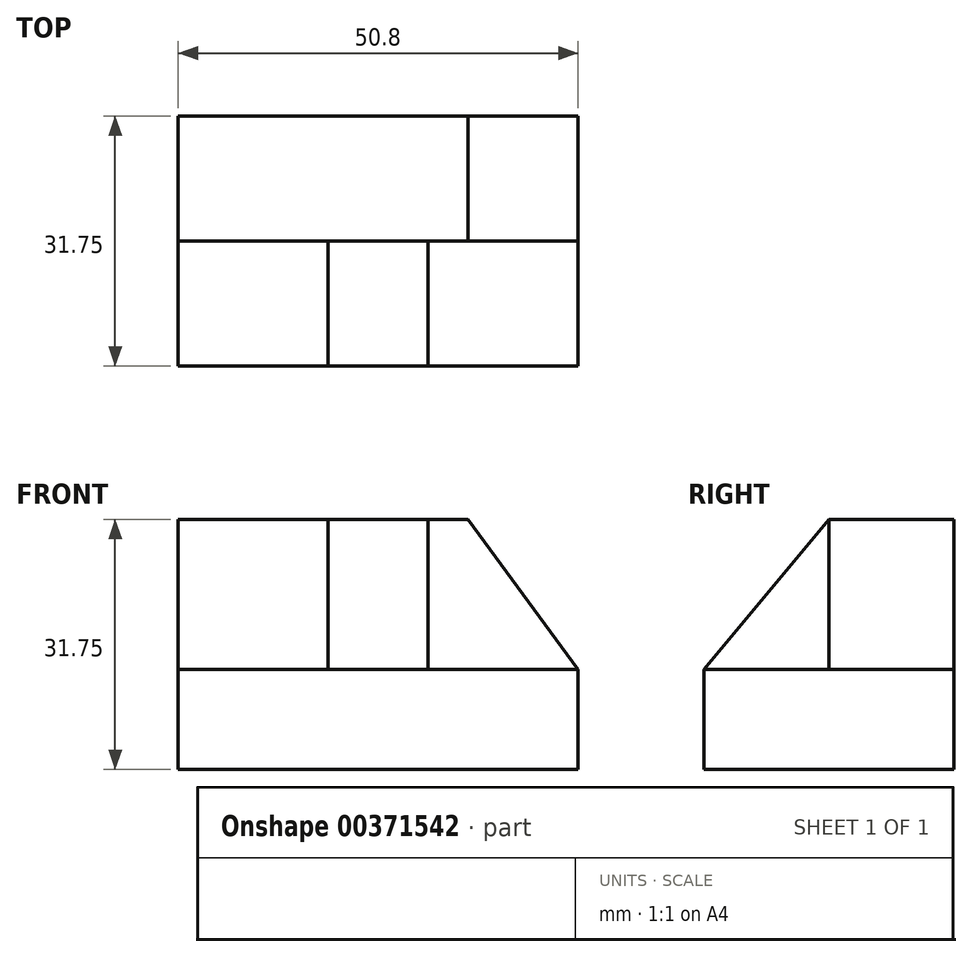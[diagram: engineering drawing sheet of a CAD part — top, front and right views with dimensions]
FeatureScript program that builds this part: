
annotation { "Feature Type Name" : "Feature", "Feature Type Description" : "" }
export const myFeature = defineFeature(function(context is Context, id is Id, definition is map)
    precondition{}
    {
        {
            var Q0;
            Q0=qCreatedBy(makeId("Front.planeOp"),FACE);
            var sketch = newSketch(context, id + "F0", { "sketchPlane" : qUnion([Q0])});
            skLineSegment(sketch, "E0", {"start": v(0, 0) * mm, "end": v(50.8, 0) * mm});
            skLineSegment(sketch, "E1", {"start": v(50.8, 0) * mm, "end": v(50.8, 31.75) * mm});
            skLineSegment(sketch, "E2", {"start": v(50.8, 31.75) * mm, "end": v(0, 31.75) * mm});
            skLineSegment(sketch, "E3", {"start": v(0, 31.75) * mm, "end": v(0, 0) * mm});
            skSolve(sketch);
        }
        {
            var Q0;
            Q0 = qSketchRegion(id + "F0", true);
            extrude(context, id + "F1", {"entities" : qUnion([Q0]), "depth" : 31.75 * mm});
        }
        {
            var Q0;
            Q0=makeQuery(id+"F1.opExtrude","SWEPT_FACE",FACE,{"disambiguationData":[OSD([sQuery(id+"F0.wireOp",EDGE,"E1")])]});
            var sketch = newSketch(context, id + "F2", { "sketchPlane" : qUnion([Q0])});
            skLineSegment(sketch, "E4", {"start": v(-15.88, 31.75) * mm, "end": v(-15.88, 12.7) * mm});
            skLineSegment(sketch, "E5", {"start": v(-15.88, 12.7) * mm, "end": v(-31.75, 12.7) * mm});
            skLineSegment(sketch, "E6", {"start": v(-31.75, 12.7) * mm, "end": v(-31.75, 31.75) * mm});
            skLineSegment(sketch, "E7", {"start": v(-31.75, 31.75) * mm, "end": v(-15.88, 31.75) * mm});
            skSolve(sketch);
        }
        {
            var Q0;
            Q0=makeQuery(id+"F1.opExtrude","SWEPT_FACE",FACE,{"disambiguationData":[OSD([sQuery(id+"F0.wireOp",EDGE,"E3")])]});
            var sketch = newSketch(context, id + "F3", { "sketchPlane" : qUnion([Q0])});
            skLineSegment(sketch, "E8", {"start": v(15.88, 31.75) * mm, "end": v(15.88, 12.7) * mm});
            skLineSegment(sketch, "E9", {"start": v(15.88, 12.7) * mm, "end": v(31.75, 12.7) * mm});
            skLineSegment(sketch, "E10", {"start": v(31.75, 12.7) * mm, "end": v(31.75, 31.75) * mm});
            skLineSegment(sketch, "E11", {"start": v(31.75, 31.75) * mm, "end": v(15.88, 31.75) * mm});
            skSolve(sketch);
        }
        {
            var Q0;
            Q0 = qSketchRegion(id + "F3", true);
            extrude(context, id + "F4", {"entities" : qUnion([Q0]), "operationType" : NewBodyOperationType.REMOVE, "oppositeDirection" : true, "depth" : 19.05 * mm});
        }
        {
            var Q0;
            Q0=makeQuery(id+"F2.imprint","IMPRINT",FACE,{"disambiguationData":[TD([[makeQuery(id+"F2.imprint","IMPRINT",EDGE,{"derivedFrom":sQuery(id+"F2.wireOp",EDGE,"E4")}),-1.0]])]});
            extrude(context, id + "F5", {"entities" : qUnion([Q0]), "operationType" : NewBodyOperationType.REMOVE, "oppositeDirection" : true, "depth" : 19.05 * mm});
        }
        {
            var Q0;
            Q0=makeQuery(id+"F5.boolean.opBoolean","COPY",FACE,{"derivedFrom":makeQuery(id+"F5.opExtrude","CAP_FACE",FACE,{"disambiguationData":[OSD([sQuery(id+"F2.wireOp",EDGE,"E4"),sQuery(id+"F2.wireOp",EDGE,"E5"),sQuery(id+"F2.wireOp",EDGE,"E6"),sQuery(id+"F2.wireOp",EDGE,"E7")])],"isStart":false})});
            var sketch = newSketch(context, id + "F6", { "sketchPlane" : qUnion([Q0])});
            skLineSegment(sketch, "E12", {"start": v(-31.75, 12.7) * mm, "end": v(-15.88, 31.75) * mm});
            skSolve(sketch);
        }
        {
            var Q0;
            Q0 = qSketchRegion(id + "F6", true);
            var Q1;
            Q1=makeQuery(id+"F6.imprint","IMPRINT",FACE,{"disambiguationData":[TD([[makeQuery(id+"F6.imprint","IMPRINT",EDGE,{"derivedFrom":sQuery(id+"F6.wireOp",EDGE,"E12")}),1.0]])]});
            extrude(context, id + "F7", {"entities" : qUnion([Q0, Q1]), "operationType" : NewBodyOperationType.REMOVE, "oppositeDirection" : true, "depth" : 25.4 * mm});
        }
        {
            var Q0;
            Q0=makeQuery(id+"F5.boolean.opBoolean","COPY",FACE,{"derivedFrom":makeQuery(id+"F5.opExtrude","SWEPT_FACE",FACE,{"disambiguationData":[OSD([sQuery(id+"F2.wireOp",EDGE,"E4")])]})});
            var sketch = newSketch(context, id + "F8", { "sketchPlane" : qUnion([Q0])});
            skLineSegment(sketch, "E13", {"start": v(50.8, 12.7) * mm, "end": v(36.83, 31.75) * mm});
            skSolve(sketch);
        }
        {
            var Q0;
            Q0 = qSketchRegion(id + "F8", true);
            var Q1;
            {var subQ0=sQuery(id+"F8.wireOp",EDGE,"E13");Q1=makeQuery(id+"F8.imprint","IMPRINT",FACE,{"disambiguationData":[TD([[makeQuery(id+"F8.imprint","IMPRINT",EDGE,{"derivedFrom":subQ0}),-1.0]])]});}
            extrude(context, id + "F9", {"entities" : qUnion([Q0, Q1]), "operationType" : NewBodyOperationType.REMOVE, "oppositeDirection" : true, "depth" : 25.4 * mm});
        }
    });
